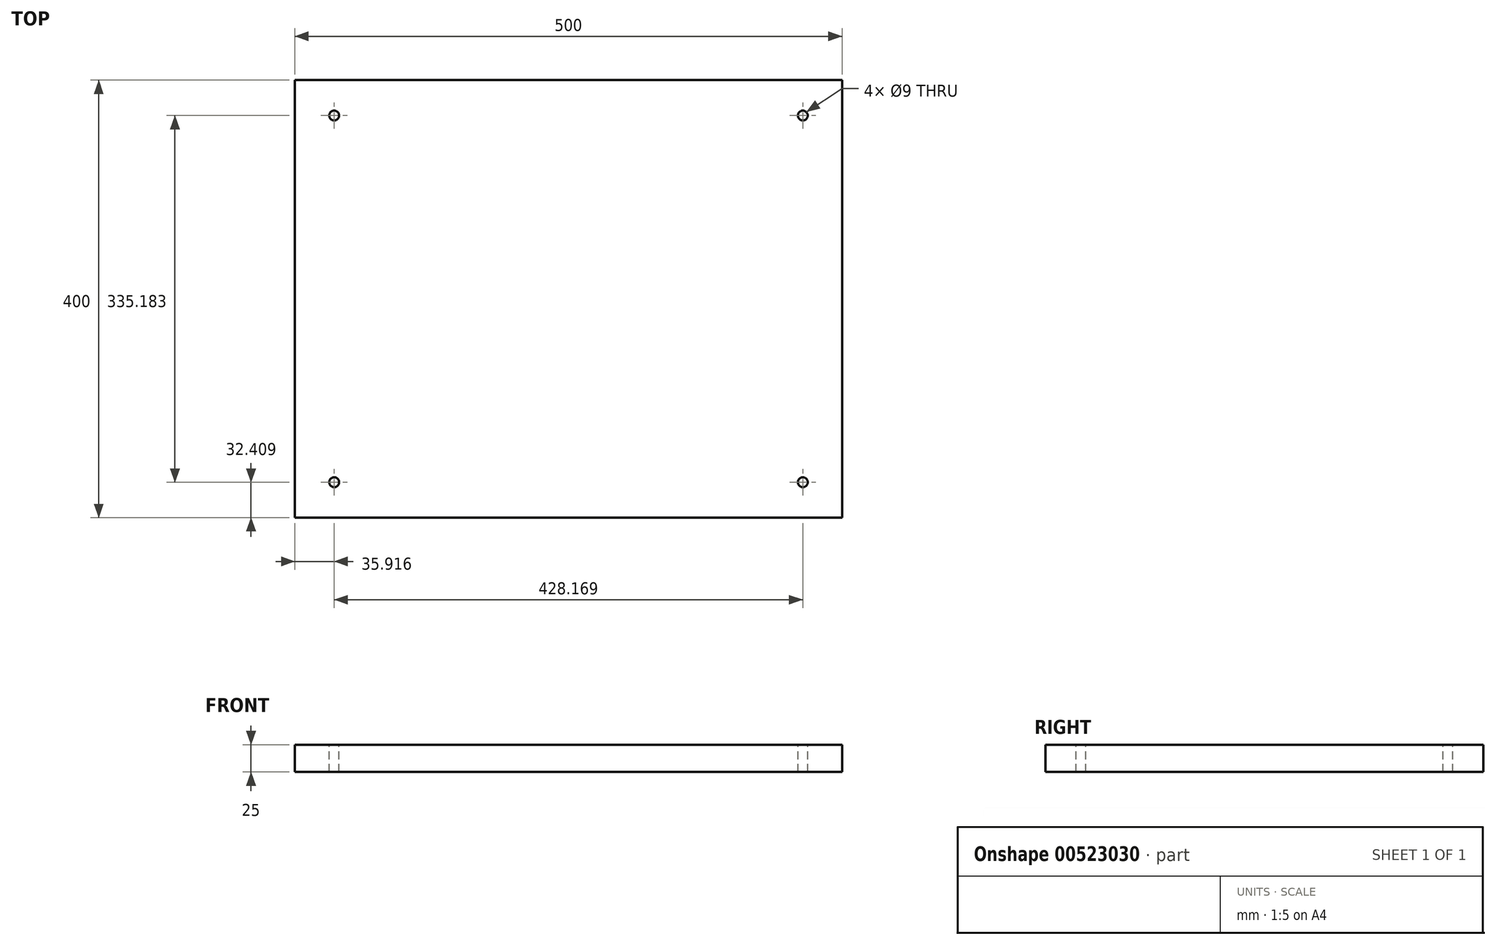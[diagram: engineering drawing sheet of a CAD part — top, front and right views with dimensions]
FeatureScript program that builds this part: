
annotation { "Feature Type Name" : "Feature", "Feature Type Description" : "" }
export const myFeature = defineFeature(function(context is Context, id is Id, definition is map)
    precondition{}
    {
        {
            var Q0;
            Q0=qCreatedBy(makeId("Top.planeOp"),FACE);
            var sketch = newSketch(context, id + "F0", { "sketchPlane" : qUnion([Q0])});
            skLineSegment(sketch, "E0.bottom", {"start": v(250, 200) * mm, "end": v(-250, 200) * mm});
            skLineSegment(sketch, "E0.top", {"start": v(250, -200) * mm, "end": v(-250, -200) * mm});
            skLineSegment(sketch, "E0.left", {"start": v(250, 200) * mm, "end": v(250, -200) * mm});
            skLineSegment(sketch, "E0.right", {"start": v(-250, 200) * mm, "end": v(-250, -200) * mm});
            skPoint(sketch, "E0.middle", {"position": v(0, 0) * mm});
            skSolve(sketch);
        }
        {
            var Q0;
            Q0=makeQuery(id+"F0.imprint","IMPRINT",FACE,{"disambiguationData":[TD([[makeQuery(id+"F0.imprint","IMPRINT",EDGE,{"derivedFrom":sQuery(id+"F0.wireOp",EDGE,"E0.bottom")}),1.0]])]});
            extrude(context, id + "F1", {"entities" : qUnion([Q0]), "depth" : 25 * mm, "offsetDistance" : 25 * mm});
        }
        {
            var Q0;
            Q0=makeQuery(id+"F1.opExtrude","CAP_FACE",FACE,{"disambiguationData":[OSD([sQuery(id+"F0.wireOp",EDGE,"E0.bottom"),sQuery(id+"F0.wireOp",EDGE,"E0.top"),sQuery(id+"F0.wireOp",EDGE,"E0.left"),sQuery(id+"F0.wireOp",EDGE,"E0.right")])],"isStart":false});
            var sketch = newSketch(context, id + "F2", { "sketchPlane" : qUnion([Q0])});
            skCircle(sketch, "E1", {"center": v(-214.08, 167.6) * mm, "radius": 4.5 * mm});
            skCircle(sketch, "E2.MirrorC", {"center": v(214.08, 167.6) * mm, "radius": 4.5 * mm});
            skCircle(sketch, "E3.MirrorC", {"center": v(-214.08, -167.6) * mm, "radius": 4.5 * mm});
            skCircle(sketch, "E4.MirrorC", {"center": v(214.08, -167.6) * mm, "radius": 4.5 * mm});
            skLineSegment(sketch, "E5", {"start": v(-214.08, -167.6) * mm, "end": v(214.08, -167.6) * mm});
            skSolve(sketch);
        }
        {
            var Q0;
            Q0 = qSketchRegion(id + "F2", true);
            extrude(context, id + "F3", {"entities" : qUnion([Q0]), "operationType" : NewBodyOperationType.REMOVE, "endBound" : BoundingType.THROUGH_ALL, "oppositeDirection" : true, "depth" : 25 * mm, "offsetDistance" : 25 * mm});
        }
    });
